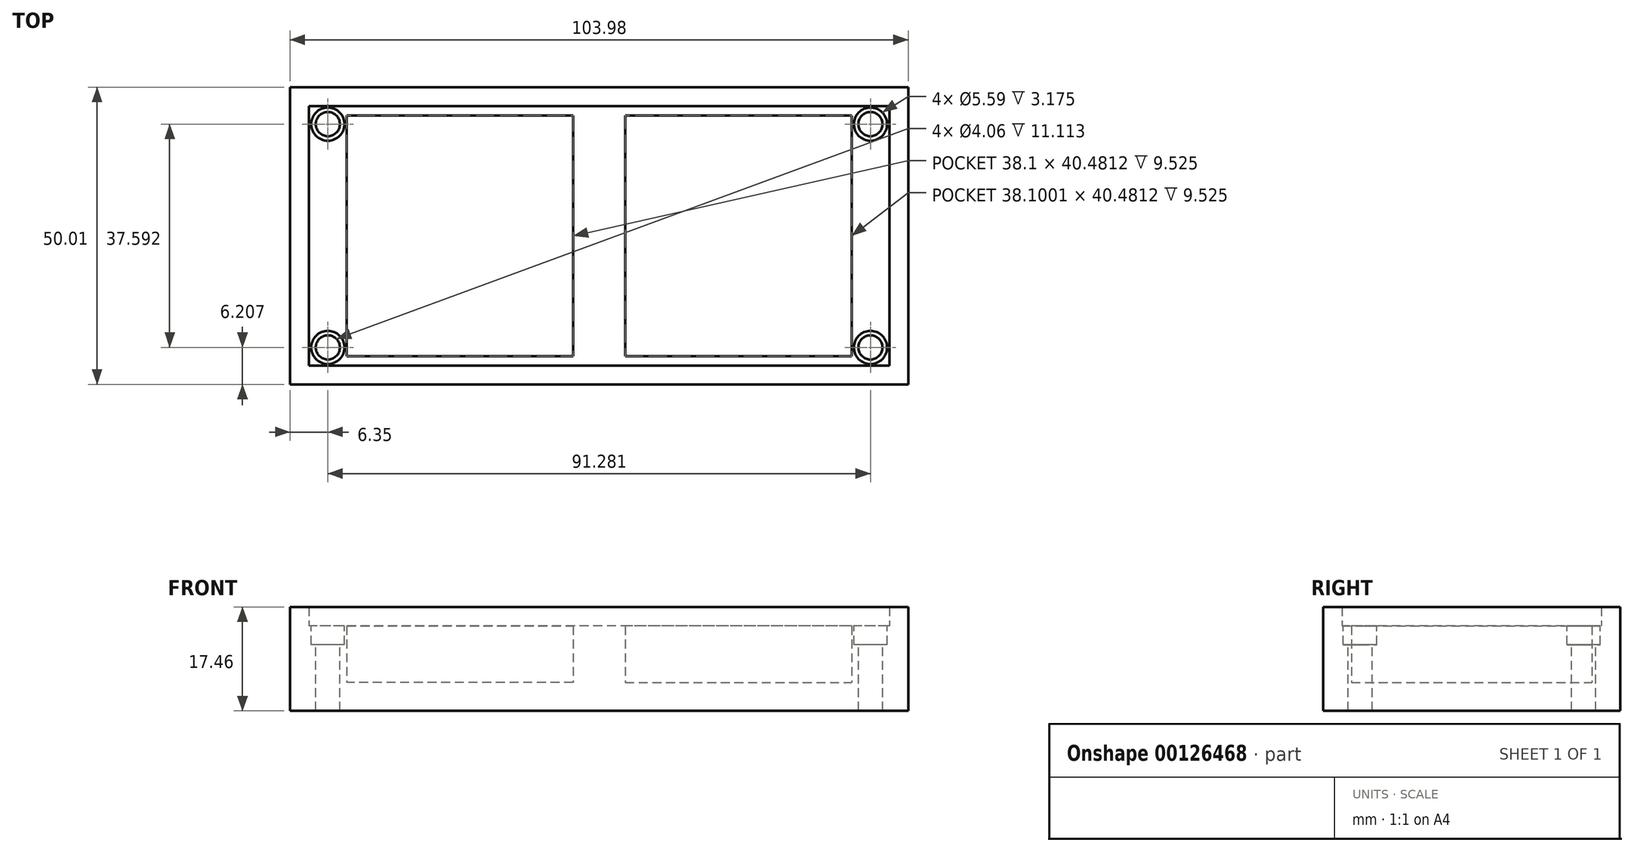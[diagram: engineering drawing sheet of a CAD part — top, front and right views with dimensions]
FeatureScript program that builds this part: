
annotation { "Feature Type Name" : "Feature", "Feature Type Description" : "" }
export const myFeature = defineFeature(function(context is Context, id is Id, definition is map)
    precondition{}
    {
        {
            var Q0;
            Q0=qCreatedBy(makeId("Top.planeOp"),FACE);
            var sketch = newSketch(context, id + "F0", { "sketchPlane" : qUnion([Q0])});
            skLineSegment(sketch, "E0.bottom", {"start": v(0, 0) * mm, "end": v(103.98, 0) * mm});
            skLineSegment(sketch, "E0.top", {"start": v(0, 50) * mm, "end": v(103.98, 50) * mm});
            skLineSegment(sketch, "E0.left", {"start": v(0, 0) * mm, "end": v(0, 50) * mm});
            skLineSegment(sketch, "E0.right", {"start": v(103.98, 0) * mm, "end": v(103.98, 50) * mm});
            skLineSegment(sketch, "E1", {"start": v(52, 50) * mm, "end": v(52, 0) * mm, "construction": true});
            skLineSegment(sketch, "E2", {"start": v(0, 25) * mm, "end": v(103.98, 25) * mm, "construction": true});
            skLineSegment(sketch, "E3.bottom", {"start": v(3.17, 46.83) * mm, "end": v(100.8, 46.83) * mm});
            skLineSegment(sketch, "E3.top", {"start": v(3.17, 3.18) * mm, "end": v(100.8, 3.18) * mm});
            skLineSegment(sketch, "E3.left", {"start": v(3.17, 46.83) * mm, "end": v(3.17, 3.18) * mm});
            skLineSegment(sketch, "E3.right", {"start": v(100.8, 46.83) * mm, "end": v(100.8, 3.18) * mm});
            skPoint(sketch, "E3.middle", {"position": v(52, 25) * mm});
            skLineSegment(sketch, "E4.bottom", {"start": v(9.52, 45.24) * mm, "end": v(47.62, 45.24) * mm});
            skLineSegment(sketch, "E4.top", {"start": v(9.52, 4.76) * mm, "end": v(47.62, 4.76) * mm});
            skLineSegment(sketch, "E4.left", {"start": v(9.52, 45.24) * mm, "end": v(9.52, 4.76) * mm});
            skLineSegment(sketch, "E4.right", {"start": v(47.62, 45.24) * mm, "end": v(47.62, 4.76) * mm});
            skPoint(sketch, "E4.middle", {"position": v(28.57, 25) * mm});
            skLineSegment(sketch, "E5.MirrorCS", {"start": v(94.46, 45.24) * mm, "end": v(56.36, 45.24) * mm});
            skLineSegment(sketch, "E6.MirrorCS", {"start": v(56.36, 45.24) * mm, "end": v(56.36, 4.76) * mm});
            skLineSegment(sketch, "E7.MirrorCS", {"start": v(94.46, 45.24) * mm, "end": v(94.46, 4.76) * mm});
            skLineSegment(sketch, "E8.MirrorCS", {"start": v(94.46, 4.76) * mm, "end": v(56.36, 4.76) * mm});
            skSolve(sketch);
        }
        {
            var Q0;
            Q0 = qSketchRegion(id + "F0", true);
            var Q1;
            Q1=makeQuery(id+"F0.imprint","IMPRINT",FACE,{"disambiguationData":[TD([[makeQuery(id+"F0.imprint","IMPRINT",EDGE,{"derivedFrom":sQuery(id+"F0.wireOp",EDGE,"E3.bottom")}),-1.0]])]});
            var Q2;
            Q2=makeQuery(id+"F0.imprint","IMPRINT",FACE,{"disambiguationData":[TD([[makeQuery(id+"F0.imprint","IMPRINT",EDGE,{"derivedFrom":sQuery(id+"F0.wireOp",EDGE,"E4.bottom")}),-1.0]])]});
            var Q3;
            Q3=makeQuery(id+"F0.imprint","IMPRINT",FACE,{"disambiguationData":[TD([[makeQuery(id+"F0.imprint","IMPRINT",EDGE,{"derivedFrom":sQuery(id+"F0.wireOp",EDGE,"E5.MirrorCS")}),1.0]])]});
            extrude(context, id + "F1", {"entities" : qUnion([Q0, Q1, Q2, Q3]), "depth" : 4.76 * mm});
        }
        {
            var Q0;
            Q0=makeQuery(id+"F0.imprint","IMPRINT",FACE,{"disambiguationData":[TD([[makeQuery(id+"F0.imprint","IMPRINT",EDGE,{"derivedFrom":sQuery(id+"F0.wireOp",EDGE,"E0.bottom")}),1.0]])]});
            var Q1;
            Q1=makeQuery(id+"F0.imprint","IMPRINT",FACE,{"disambiguationData":[TD([[makeQuery(id+"F0.imprint","IMPRINT",EDGE,{"derivedFrom":sQuery(id+"F0.wireOp",EDGE,"E3.bottom")}),-1.0]])]});
            extrude(context, id + "F2", {"entities" : qUnion([Q0, Q1]), "operationType" : NewBodyOperationType.ADD, "depth" : 14.29 * mm});
        }
        {
            var Q0;
            Q0=makeQuery(id+"F0.imprint","IMPRINT",FACE,{"disambiguationData":[TD([[makeQuery(id+"F0.imprint","IMPRINT",EDGE,{"derivedFrom":sQuery(id+"F0.wireOp",EDGE,"E0.bottom")}),1.0]])]});
            extrude(context, id + "F3", {"entities" : qUnion([Q0]), "operationType" : NewBodyOperationType.ADD, "depth" : 17.46 * mm});
        }
        {
            var Q0;
            Q0=makeQuery(id+"F2.opExtrude","CAP_FACE",FACE,{"disambiguationData":[OSD([sQuery(id+"F0.wireOp",EDGE,"E0.bottom"),sQuery(id+"F0.wireOp",EDGE,"E0.top"),sQuery(id+"F0.wireOp",EDGE,"E0.left"),sQuery(id+"F0.wireOp",EDGE,"E0.right"),sQuery(id+"F0.wireOp",EDGE,"E4.bottom"),sQuery(id+"F0.wireOp",EDGE,"E4.top"),sQuery(id+"F0.wireOp",EDGE,"E4.left"),sQuery(id+"F0.wireOp",EDGE,"E4.right"),sQuery(id+"F0.wireOp",EDGE,"E5.MirrorCS"),sQuery(id+"F0.wireOp",EDGE,"E6.MirrorCS"),sQuery(id+"F0.wireOp",EDGE,"E7.MirrorCS"),sQuery(id+"F0.wireOp",EDGE,"E8.MirrorCS")])],"isStart":false});
            var sketch = newSketch(context, id + "F4", { "sketchPlane" : qUnion([Q0])});
            skLineSegment(sketch, "E9", {"start": v(52, 46.83) * mm, "end": v(52, 3.18) * mm, "construction": true});
            skLineSegment(sketch, "E10", {"start": v(3.17, 25) * mm, "end": v(9.52, 25) * mm, "construction": true});
            skLineSegment(sketch, "E11", {"start": v(3.17, 25) * mm, "end": v(100.8, 25) * mm, "construction": true});
            skPoint(sketch, "E12", {"position": v(6.35, 43.8) * mm});
            skPoint(sketch, "E12.positionSnap0", {"position": v(6.35, 25) * mm});
            skCircle(sketch, "E13", {"center": v(6.35, 43.8) * mm, "radius": 2.03 * mm});
            skCircle(sketch, "E14", {"center": v(6.35, 43.8) * mm, "radius": 2.8 * mm});
            skPoint(sketch, "E15.MirrorP", {"position": v(6.35, 6.2) * mm});
            skCircle(sketch, "E16.MirrorC", {"center": v(6.35, 6.2) * mm, "radius": 2.03 * mm});
            skCircle(sketch, "E17.MirrorC", {"center": v(6.35, 6.2) * mm, "radius": 2.8 * mm});
            skPoint(sketch, "E18.MirrorP", {"position": v(97.63, 43.8) * mm});
            skCircle(sketch, "E19.MirrorC", {"center": v(97.63, 43.8) * mm, "radius": 2.03 * mm});
            skCircle(sketch, "E20.MirrorC", {"center": v(97.63, 43.8) * mm, "radius": 2.8 * mm});
            skPoint(sketch, "E21.MirrorP", {"position": v(97.63, 6.2) * mm});
            skCircle(sketch, "E22.MirrorC", {"center": v(97.63, 6.2) * mm, "radius": 2.03 * mm});
            skCircle(sketch, "E23.MirrorC", {"center": v(97.63, 6.2) * mm, "radius": 2.8 * mm});
            skSolve(sketch);
        }
        {
            var Q0;
            Q0 = qSketchRegion(id + "F4", true);
            extrude(context, id + "F5", {"entities" : qUnion([Q0]), "operationType" : NewBodyOperationType.REMOVE, "oppositeDirection" : true, "depth" : 3.17 * mm});
        }
        {
            var Q0;
            Q0=makeQuery(id+"F5.boolean.opBoolean","SPLIT",FACE,{"disambiguationData":[TD([makeQuery(id+"F5.opExtrude","SWEPT_FACE",FACE,{"disambiguationData":[OSD([sQuery(id+"F4.wireOp",EDGE,"E13")])]})])],"derivedFrom":makeQuery(id+"F2.opExtrude","CAP_FACE",FACE,{"disambiguationData":[OSD([sQuery(id+"F0.wireOp",EDGE,"E0.bottom"),sQuery(id+"F0.wireOp",EDGE,"E0.top"),sQuery(id+"F0.wireOp",EDGE,"E0.left"),sQuery(id+"F0.wireOp",EDGE,"E0.right"),sQuery(id+"F0.wireOp",EDGE,"E4.bottom"),sQuery(id+"F0.wireOp",EDGE,"E4.top"),sQuery(id+"F0.wireOp",EDGE,"E4.left"),sQuery(id+"F0.wireOp",EDGE,"E4.right"),sQuery(id+"F0.wireOp",EDGE,"E5.MirrorCS"),sQuery(id+"F0.wireOp",EDGE,"E6.MirrorCS"),sQuery(id+"F0.wireOp",EDGE,"E7.MirrorCS"),sQuery(id+"F0.wireOp",EDGE,"E8.MirrorCS")])],"isStart":false})});
            var Q1;
            Q1=makeQuery(id+"F5.boolean.opBoolean","SPLIT",FACE,{"disambiguationData":[TD([makeQuery(id+"F5.opExtrude","SWEPT_FACE",FACE,{"disambiguationData":[OSD([sQuery(id+"F4.wireOp",EDGE,"E19.MirrorC")])]})])],"derivedFrom":makeQuery(id+"F2.opExtrude","CAP_FACE",FACE,{"disambiguationData":[OSD([sQuery(id+"F0.wireOp",EDGE,"E0.bottom"),sQuery(id+"F0.wireOp",EDGE,"E0.top"),sQuery(id+"F0.wireOp",EDGE,"E0.left"),sQuery(id+"F0.wireOp",EDGE,"E0.right"),sQuery(id+"F0.wireOp",EDGE,"E4.bottom"),sQuery(id+"F0.wireOp",EDGE,"E4.top"),sQuery(id+"F0.wireOp",EDGE,"E4.left"),sQuery(id+"F0.wireOp",EDGE,"E4.right"),sQuery(id+"F0.wireOp",EDGE,"E5.MirrorCS"),sQuery(id+"F0.wireOp",EDGE,"E6.MirrorCS"),sQuery(id+"F0.wireOp",EDGE,"E7.MirrorCS"),sQuery(id+"F0.wireOp",EDGE,"E8.MirrorCS")])],"isStart":false})});
            var Q2;
            Q2=makeQuery(id+"F5.boolean.opBoolean","SPLIT",FACE,{"disambiguationData":[TD([makeQuery(id+"F5.opExtrude","SWEPT_FACE",FACE,{"disambiguationData":[OSD([sQuery(id+"F4.wireOp",EDGE,"E22.MirrorC")])]})])],"derivedFrom":makeQuery(id+"F2.opExtrude","CAP_FACE",FACE,{"disambiguationData":[OSD([sQuery(id+"F0.wireOp",EDGE,"E0.bottom"),sQuery(id+"F0.wireOp",EDGE,"E0.top"),sQuery(id+"F0.wireOp",EDGE,"E0.left"),sQuery(id+"F0.wireOp",EDGE,"E0.right"),sQuery(id+"F0.wireOp",EDGE,"E4.bottom"),sQuery(id+"F0.wireOp",EDGE,"E4.top"),sQuery(id+"F0.wireOp",EDGE,"E4.left"),sQuery(id+"F0.wireOp",EDGE,"E4.right"),sQuery(id+"F0.wireOp",EDGE,"E5.MirrorCS"),sQuery(id+"F0.wireOp",EDGE,"E6.MirrorCS"),sQuery(id+"F0.wireOp",EDGE,"E7.MirrorCS"),sQuery(id+"F0.wireOp",EDGE,"E8.MirrorCS")])],"isStart":false})});
            var Q3;
            Q3=makeQuery(id+"F5.boolean.opBoolean","SPLIT",FACE,{"disambiguationData":[TD([makeQuery(id+"F5.opExtrude","SWEPT_FACE",FACE,{"disambiguationData":[OSD([sQuery(id+"F4.wireOp",EDGE,"E16.MirrorC")])]})])],"derivedFrom":makeQuery(id+"F2.opExtrude","CAP_FACE",FACE,{"disambiguationData":[OSD([sQuery(id+"F0.wireOp",EDGE,"E0.bottom"),sQuery(id+"F0.wireOp",EDGE,"E0.top"),sQuery(id+"F0.wireOp",EDGE,"E0.left"),sQuery(id+"F0.wireOp",EDGE,"E0.right"),sQuery(id+"F0.wireOp",EDGE,"E4.bottom"),sQuery(id+"F0.wireOp",EDGE,"E4.top"),sQuery(id+"F0.wireOp",EDGE,"E4.left"),sQuery(id+"F0.wireOp",EDGE,"E4.right"),sQuery(id+"F0.wireOp",EDGE,"E5.MirrorCS"),sQuery(id+"F0.wireOp",EDGE,"E6.MirrorCS"),sQuery(id+"F0.wireOp",EDGE,"E7.MirrorCS"),sQuery(id+"F0.wireOp",EDGE,"E8.MirrorCS")])],"isStart":false})});
            var Q4;
            Q4=makeQuery(id+"F1.opExtrude","CAP_FACE",FACE,{"disambiguationData":[OSD([sQuery(id+"F0.wireOp",EDGE,"E0.bottom"),sQuery(id+"F0.wireOp",EDGE,"E0.top"),sQuery(id+"F0.wireOp",EDGE,"E0.left"),sQuery(id+"F0.wireOp",EDGE,"E0.right")])],"isStart":true});
            extrude(context, id + "F6", {"entities" : qUnion([Q0, Q1, Q2, Q3]), "operationType" : NewBodyOperationType.REMOVE, "endBound" : BoundingType.UP_TO_SURFACE, "oppositeDirection" : true, "endBoundEntityFace" : qUnion([Q4]), "depth" : 25.4 * mm});
        }
    });
